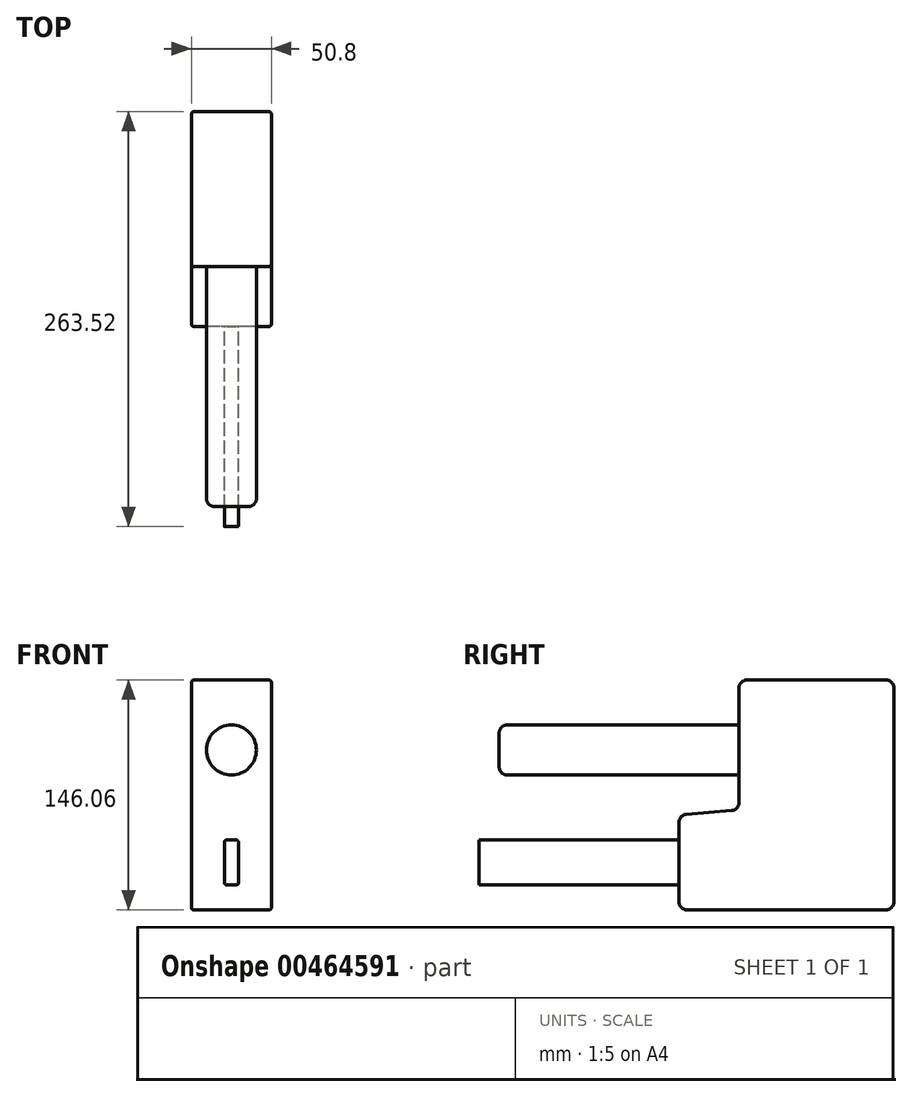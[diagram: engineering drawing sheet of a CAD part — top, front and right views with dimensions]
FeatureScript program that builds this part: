
annotation { "Feature Type Name" : "Feature", "Feature Type Description" : "" }
export const myFeature = defineFeature(function(context is Context, id is Id, definition is map)
    precondition{}
    {
        {
            var Q0;
            Q0=qCreatedBy(makeId("Right.planeOp"),FACE);
            var sketch = newSketch(context, id + "F0", { "sketchPlane" : qUnion([Q0])});
            skLineSegment(sketch, "E0", {"start": v(68.26, 73.02) * mm, "end": v(68.26, -73.02) * mm});
            skLineSegment(sketch, "E1", {"start": v(68.26, -73.02) * mm, "end": v(-68.26, -73.03) * mm});
            skLineSegment(sketch, "E2", {"start": v(-68.26, -73.03) * mm, "end": v(-68.26, -12.7) * mm});
            skLineSegment(sketch, "E3", {"start": v(-68.26, -12.7) * mm, "end": v(-30.16, -9.53) * mm});
            skLineSegment(sketch, "E4", {"start": v(68.26, 73.02) * mm, "end": v(-30.16, 73.02) * mm});
            skLineSegment(sketch, "E5", {"start": v(-30.16, -9.53) * mm, "end": v(-30.16, 73.02) * mm});
            skSolve(sketch);
        }
        {
            var Q0;
            Q0=makeQuery(id+"F0.imprint","IMPRINT",FACE,{"disambiguationData":[TD([[makeQuery(id+"F0.imprint","IMPRINT",EDGE,{"derivedFrom":sQuery(id+"F0.wireOp",EDGE,"E0")}),-1.0]])]});
            extrude(context, id + "F1", {"entities" : qUnion([Q0]), "endBound" : BoundingType.SYMMETRIC, "depth" : 50.8 * mm});
        }
        {
            var Q0;
            Q0=makeQuery(id+"F1.opExtrude","SWEPT_EDGE",EDGE,{"disambiguationData":[OSD([sQuery(id+"F0.wireOp",EDGE,"E2"),sQuery(id+"F0.wireOp",EDGE,"E3")])]});
            var Q1;
            Q1=makeQuery(id+"F1.opExtrude","SWEPT_EDGE",EDGE,{"disambiguationData":[OSD([sQuery(id+"F0.wireOp",EDGE,"E3"),sQuery(id+"F0.wireOp",EDGE,"E5")])]});
            var Q2;
            Q2=makeQuery(id+"F1.opExtrude","SWEPT_EDGE",EDGE,{"disambiguationData":[OSD([sQuery(id+"F0.wireOp",EDGE,"E4"),sQuery(id+"F0.wireOp",EDGE,"E5")])]});
            var Q3;
            Q3=makeQuery(id+"F1.opExtrude","SWEPT_EDGE",EDGE,{"disambiguationData":[OSD([sQuery(id+"F0.wireOp",EDGE,"E0"),sQuery(id+"F0.wireOp",EDGE,"E4")])]});
            var Q4;
            Q4=makeQuery(id+"F1.opExtrude","SWEPT_EDGE",EDGE,{"disambiguationData":[OSD([sQuery(id+"F0.wireOp",EDGE,"E0"),sQuery(id+"F0.wireOp",EDGE,"E1")])]});
            var Q5;
            Q5=makeQuery(id+"F1.opExtrude","SWEPT_EDGE",EDGE,{"disambiguationData":[OSD([sQuery(id+"F0.wireOp",EDGE,"E1"),sQuery(id+"F0.wireOp",EDGE,"E2")])]});
            fillet(context, id + "F2", {"entities" : qUnion([Q0, Q1, Q2, Q3, Q4, Q5]), "radius" : 5.08 * mm, "tangentPropagation" : true, "allowEdgeOverflow" : false});
        }
        {
            var Q0;
            Q0=makeQuery(id+"F1.opExtrude","CAP_EDGE",EDGE,{"disambiguationData":[OSD([sQuery(id+"F0.wireOp",EDGE,"E3")])],"isStart":false});
            var Q1;
            Q1=makeQuery(id+"F1.opExtrude","CAP_EDGE",EDGE,{"disambiguationData":[OSD([sQuery(id+"F0.wireOp",EDGE,"E3")])],"isStart":true});
            fillet(context, id + "F3", {"entities" : qUnion([Q0, Q1]), "radius" : 1.59 * mm, "tangentPropagation" : true, "allowEdgeOverflow" : false});
        }
        {
            var Q0;
            Q0=makeQuery(id+"F1.opExtrude","SWEPT_FACE",FACE,{"disambiguationData":[OSD([sQuery(id+"F0.wireOp",EDGE,"E2")])]});
            var sketch = newSketch(context, id + "F4", { "sketchPlane" : qUnion([Q0])});
            skLineSegment(sketch, "E6.bottom", {"start": v(-4.5, -28.58) * mm, "end": v(4.5, -28.58) * mm});
            skLineSegment(sketch, "E6.top", {"start": v(-4.5, -57.15) * mm, "end": v(4.5, -57.15) * mm});
            skLineSegment(sketch, "E6.left", {"start": v(-4.5, -28.58) * mm, "end": v(-4.5, -57.15) * mm});
            skLineSegment(sketch, "E6.right", {"start": v(4.5, -28.58) * mm, "end": v(4.5, -57.15) * mm});
            skSolve(sketch);
        }
        {
            var Q0;
            Q0 = qSketchRegion(id + "F4", true);
            extrude(context, id + "F5", {"entities" : qUnion([Q0]), "operationType" : NewBodyOperationType.ADD, "depth" : 127 * mm});
        }
        {
            var Q0;
            Q0=makeQuery(id+"F5.opExtrude","SWEPT_EDGE",EDGE,{"disambiguationData":[OSD([sQuery(id+"F4.wireOp",EDGE,"E6.bottom"),sQuery(id+"F4.wireOp",EDGE,"E6.right")])]});
            var Q1;
            Q1=makeQuery(id+"F5.opExtrude","SWEPT_EDGE",EDGE,{"disambiguationData":[OSD([sQuery(id+"F4.wireOp",EDGE,"E6.bottom"),sQuery(id+"F4.wireOp",EDGE,"E6.left")])]});
            var Q2;
            Q2=makeQuery(id+"F5.opExtrude","SWEPT_EDGE",EDGE,{"disambiguationData":[OSD([sQuery(id+"F4.wireOp",EDGE,"E6.top"),sQuery(id+"F4.wireOp",EDGE,"E6.right")])]});
            var Q3;
            Q3=makeQuery(id+"F5.opExtrude","SWEPT_EDGE",EDGE,{"disambiguationData":[OSD([sQuery(id+"F4.wireOp",EDGE,"E6.top"),sQuery(id+"F4.wireOp",EDGE,"E6.left")])]});
            fillet(context, id + "F6", {"entities" : qUnion([Q0, Q1, Q2, Q3]), "radius" : 1.52 * mm, "tangentPropagation" : true, "allowEdgeOverflow" : false});
        }
        {
            var Q0;
            Q0=makeQuery(id+"F1.opExtrude","SWEPT_FACE",FACE,{"disambiguationData":[OSD([sQuery(id+"F0.wireOp",EDGE,"E5")])]});
            var sketch = newSketch(context, id + "F7", { "sketchPlane" : qUnion([Q0])});
            skCircle(sketch, "E7", {"center": v(0, 28.57) * mm, "radius": 15.88 * mm});
            skSolve(sketch);
        }
        {
            var Q0;
            Q0 = qSketchRegion(id + "F7", true);
            extrude(context, id + "F8", {"entities" : qUnion([Q0]), "operationType" : NewBodyOperationType.ADD, "depth" : 152.4 * mm});
        }
        {
            var Q0;
            Q0=makeQuery(id+"F8.opExtrude","CAP_EDGE",EDGE,{"disambiguationData":[OSD([sQuery(id+"F7.wireOp",EDGE,"E7")])],"isStart":false});
            fillet(context, id + "F9", {"entities" : qUnion([Q0]), "radius" : 5.08 * mm, "tangentPropagation" : true, "allowEdgeOverflow" : false});
        }
    });
